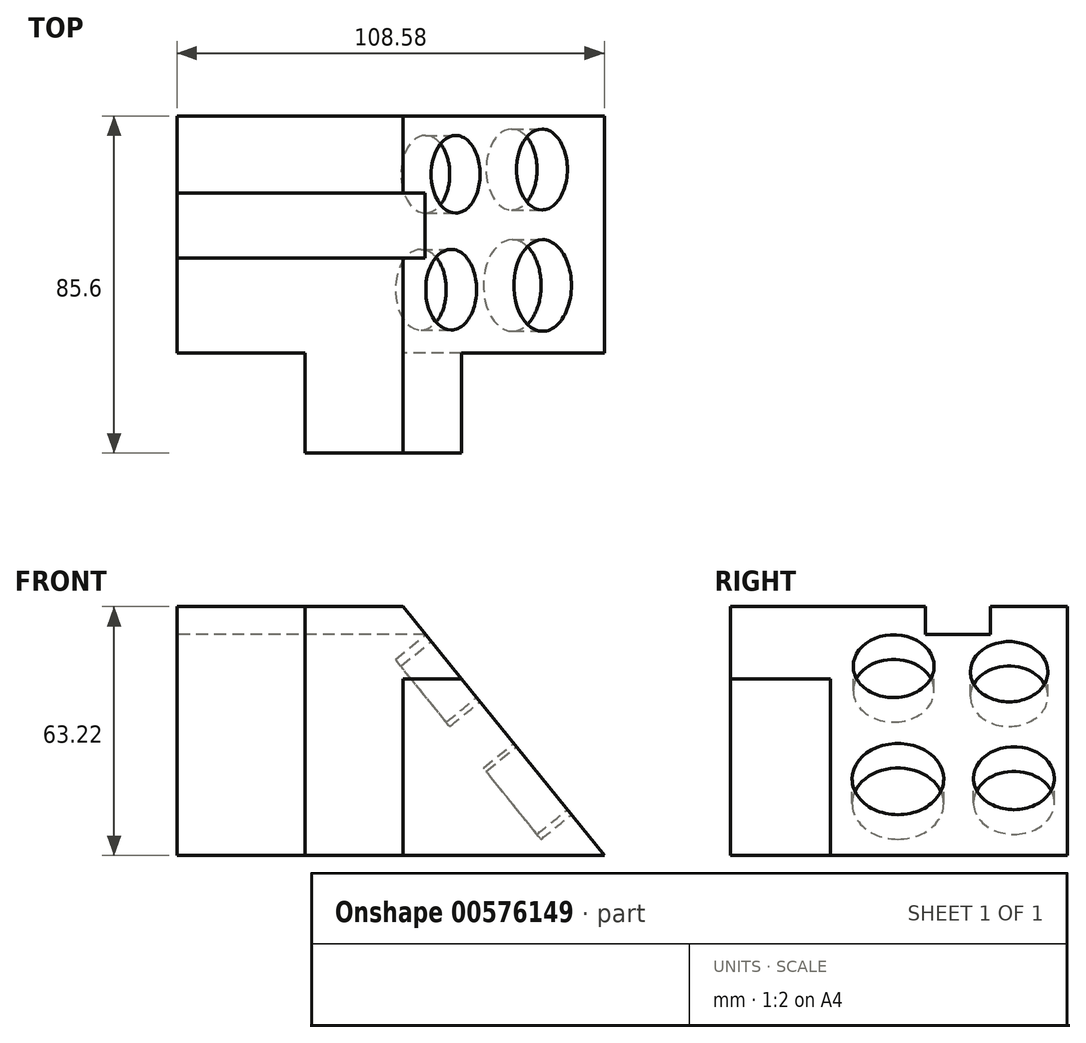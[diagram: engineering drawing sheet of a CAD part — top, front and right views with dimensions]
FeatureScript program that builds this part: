
annotation { "Feature Type Name" : "Feature", "Feature Type Description" : "" }
export const myFeature = defineFeature(function(context is Context, id is Id, definition is map)
    precondition{}
    {
        {
            var Q0;
            Q0=qCreatedBy(makeId("Front.planeOp"),FACE);
            var sketch = newSketch(context, id + "F0", { "sketchPlane" : qUnion([Q0])});
            skLineSegment(sketch, "E0.bottom", {"start": v(0, 0) * mm, "end": v(-57.38, 0) * mm});
            skLineSegment(sketch, "E0.top", {"start": v(0, 63.22) * mm, "end": v(-57.38, 63.22) * mm});
            skLineSegment(sketch, "E0.left", {"start": v(0, 0) * mm, "end": v(0, 63.22) * mm});
            skLineSegment(sketch, "E0.right", {"start": v(-57.38, 0) * mm, "end": v(-57.38, 63.22) * mm});
            skLineSegment(sketch, "E1", {"start": v(0, 63.22) * mm, "end": v(51.2, 0) * mm});
            skLineSegment(sketch, "E2", {"start": v(51.2, 0) * mm, "end": v(0, 0) * mm});
            skSolve(sketch);
        }
        {
            var Q0;
            Q0 = qSketchRegion(id + "F0", true);
            extrude(context, id + "F1", {"entities" : qUnion([Q0]), "depth" : 60.2 * mm, "offsetDistance" : 25.4 * mm});
        }
        {
            var Q0;
            Q0=makeQuery(id+"F1.opExtrude","SWEPT_FACE",FACE,{"disambiguationData":[OSD([sQuery(id+"F0.wireOp",EDGE,"E1")])]});
            var sketch = newSketch(context, id + "F2", { "sketchPlane" : qUnion([Q0])});
            skCircle(sketch, "E3", {"center": v(-44.1, 29.63) * mm, "radius": 10.26 * mm});
            skCircle(sketch, "E4", {"center": v(-14.76, 27.82) * mm, "radius": 9.86 * mm});
            skCircle(sketch, "E5", {"center": v(-13.54, -7.01) * mm, "radius": 10.28 * mm});
            skCircle(sketch, "E6", {"center": v(-43.02, -7.28) * mm, "radius": 11.64 * mm});
            skSolve(sketch);
        }
        {
            var Q0;
            Q0 = qSketchRegion(id + "F2", true);
            extrude(context, id + "F3", {"entities" : qUnion([Q0]), "operationType" : NewBodyOperationType.REMOVE, "oppositeDirection" : true, "depth" : 9.9 * mm, "offsetDistance" : 25.4 * mm});
        }
        {
            var Q0;
            Q0=makeQuery(id+"F1.opExtrude","CAP_FACE",FACE,{"disambiguationData":[OSD([sQuery(id+"F0.wireOp",EDGE,"E0.bottom"),sQuery(id+"F0.wireOp",EDGE,"E0.top"),sQuery(id+"F0.wireOp",EDGE,"E0.right"),sQuery(id+"F0.wireOp",EDGE,"E1"),sQuery(id+"F0.wireOp",EDGE,"E2")])],"isStart":false});
            var sketch = newSketch(context, id + "F4", { "sketchPlane" : qUnion([Q0])});
            skLineSegment(sketch, "E7.bottom", {"start": v(-24.8, 63.22) * mm, "end": v(0, 63.22) * mm});
            skLineSegment(sketch, "E7.top", {"start": v(-24.8, 0) * mm, "end": v(0, 0) * mm});
            skLineSegment(sketch, "E7.left", {"start": v(-24.8, 63.22) * mm, "end": v(-24.8, 0) * mm});
            skLineSegment(sketch, "E7.right", {"start": v(0, 63.22) * mm, "end": v(0, 0) * mm});
            skLineSegment(sketch, "E8", {"start": v(0, 63.22) * mm, "end": v(14.92, 44.8) * mm});
            skLineSegment(sketch, "E9", {"start": v(14.92, 44.8) * mm, "end": v(0, 44.8) * mm});
            skLineSegment(sketch, "E10", {"start": v(0, 44.8) * mm, "end": v(0, 63.22) * mm});
            skSolve(sketch);
        }
        {
            var Q0;
            Q0 = qSketchRegion(id + "F4", true);
            extrude(context, id + "F5", {"entities" : qUnion([Q0]), "operationType" : NewBodyOperationType.ADD, "depth" : 25.4 * mm, "offsetDistance" : 25.4 * mm});
        }
        {
            var Q0;
            Q0=makeQuery(id+"F1.opExtrude","SWEPT_FACE",FACE,{"disambiguationData":[OSD([sQuery(id+"F0.wireOp",EDGE,"E0.right")])]});
            var sketch = newSketch(context, id + "F6", { "sketchPlane" : qUnion([Q0])});
            skLineSegment(sketch, "E11", {"start": v(19.57, 63.22) * mm, "end": v(19.57, 56.18) * mm});
            skLineSegment(sketch, "E12", {"start": v(19.57, 56.18) * mm, "end": v(36.02, 56.18) * mm});
            skLineSegment(sketch, "E13", {"start": v(36.02, 56.18) * mm, "end": v(36.02, 63.22) * mm});
            skLineSegment(sketch, "E14", {"start": v(36.02, 63.22) * mm, "end": v(19.57, 63.22) * mm});
            skSolve(sketch);
        }
        {
            var Q0;
            Q0 = qSketchRegion(id + "F6", true);
            extrude(context, id + "F7", {"entities" : qUnion([Q0]), "operationType" : NewBodyOperationType.REMOVE, "oppositeDirection" : true, "depth" : 208.28 * mm, "offsetDistance" : 25.4 * mm});
        }
    });
